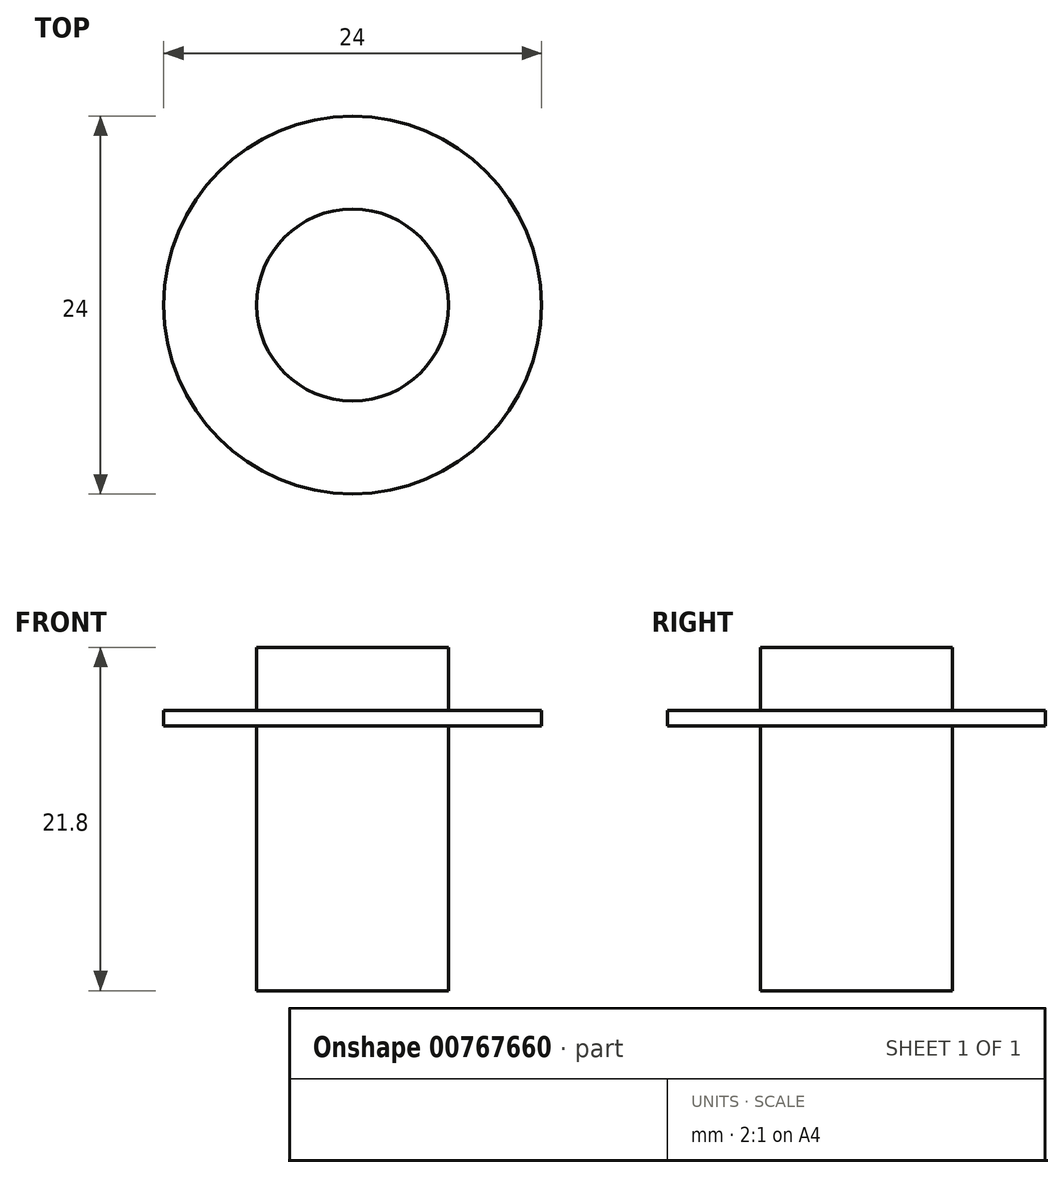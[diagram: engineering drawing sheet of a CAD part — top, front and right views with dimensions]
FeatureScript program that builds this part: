
annotation { "Feature Type Name" : "Feature", "Feature Type Description" : "" }
export const myFeature = defineFeature(function(context is Context, id is Id, definition is map)
    precondition{}
    {
        {
            var Q0;
            Q0=qCreatedBy(makeId("Front.planeOp"),FACE);
            var sketch = newSketch(context, id + "F0", { "sketchPlane" : qUnion([Q0])});
            skLineSegment(sketch, "E0", {"start": v(-6.1, 0) * mm, "end": v(-6.1, -4) * mm});
            skLineSegment(sketch, "E1", {"start": v(-6.1, -4) * mm, "end": v(-12, -4) * mm});
            skLineSegment(sketch, "E2", {"start": v(-12, -4) * mm, "end": v(-12, -5) * mm});
            skLineSegment(sketch, "E3", {"start": v(-12, -5) * mm, "end": v(-6.1, -5) * mm});
            skLineSegment(sketch, "E4", {"start": v(-6.1, -5) * mm, "end": v(-6.1, -21.8) * mm});
            skLineSegment(sketch, "E5", {"start": v(-6.1, -21.8) * mm, "end": v(0, -21.8) * mm});
            skLineSegment(sketch, "E6", {"start": v(0, -21.8) * mm, "end": v(0, 0) * mm});
            skLineSegment(sketch, "E7", {"start": v(0, 0) * mm, "end": v(-6.1, 0) * mm});
            skSolve(sketch);
        }
        {
            var Q0;
            Q0=makeQuery(id+"F0.imprint","IMPRINT",FACE,{"disambiguationData":[TD([[makeQuery(id+"F0.imprint","IMPRINT",EDGE,{"derivedFrom":sQuery(id+"F0.wireOp",EDGE,"E0")}),1.0]])]});
            var Q1;
            Q1=sQuery(id+"F0.wireOp",EDGE,"E6");
            revolve(context, id + "F1", {"surfaceOperationType" : NewSurfaceOperationType.NEW, "entities" : qUnion([Q0]), "axis" : qUnion([Q1]), "revolveType" : RevolveType.FULL});
        }
    });
